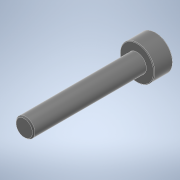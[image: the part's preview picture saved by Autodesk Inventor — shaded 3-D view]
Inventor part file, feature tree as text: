
AUTODESK INVENTOR PART (.ipt)
format: ipt  version: 2022 (Build 260153000, 153)  size: 136,704 bytes
history: native  units: in
note: dims shown in document units (in); Inventor stores cm internally (conversion verified against a paired STEP export)
features: sketch x3, extrude x2, plane x1, fillet x1, chamfer x1
ambient origin geometry x8: Origin, YZ Plane, XZ Plane, XY Plane, X Axis, Y Axis, Z Axis, Center Point
bodies: Body1 (feature_tree)
feature tree (8):
  plane  "Work Plane1"
  fillet  "Fillet1"  [1 undecoded]
  extrude  "Extrusion2"  Depth=0.0039in
  extrude  "Extrusion1"  Depth=0.7087in TaperAngle=0.0deg
  chamfer  "Chamfer1"  Distance=0.0079in
  sketch  "Sketch1"  dims[d1=0.1181in d2=0.0in d3=0.0039in]
  sketch  "Sketch2"  dims[d4=0.1181in d5=0.0in d6=0.7087in d7=0.0in d8=0.0079in d9=0.0079in d10=17.7165in]
  sketch  "Sketch3"
note: 1 required parameter value undecoded (feature->parameter linkage not recoverable at this tier; creation-order binding heuristic only, values carry confidence <= 0.55)
